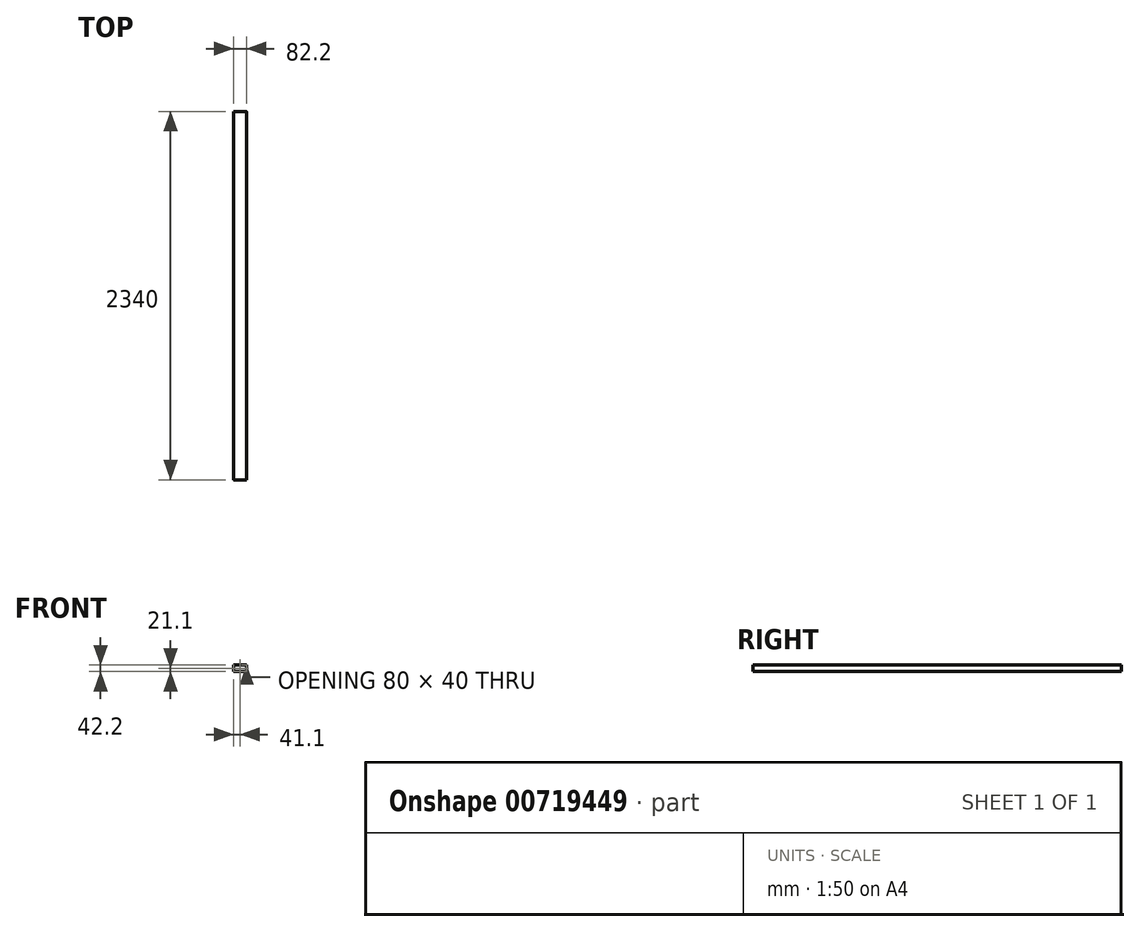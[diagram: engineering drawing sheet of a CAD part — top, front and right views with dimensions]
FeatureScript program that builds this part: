
annotation { "Feature Type Name" : "Feature", "Feature Type Description" : "" }
export const myFeature = defineFeature(function(context is Context, id is Id, definition is map)
    precondition{}
    {
        {
            var Q0;
            Q0=qCreatedBy(makeId("Front.planeOp"),FACE);
            var sketch = newSketch(context, id + "F0", { "sketchPlane" : qUnion([Q0])});
            skLineSegment(sketch, "E0.bottom", {"start": v(-35, 20) * mm, "end": v(35, 20) * mm});
            skLineSegment(sketch, "E0.top", {"start": v(-35, -20) * mm, "end": v(35, -20) * mm});
            skLineSegment(sketch, "E0.left", {"start": v(-40, 15) * mm, "end": v(-40, -15) * mm});
            skLineSegment(sketch, "E0.right", {"start": v(40, 15) * mm, "end": v(40, -15) * mm});
            skPoint(sketch, "E1.visualSharp", {"position": v(-40, 20) * mm});
            skArc(sketch, "E1.filletArc", {"start": v(-35, 20) * mm, "mid": v(-38.54, 18.54) * mm, "end": v(-40, 15) * mm});
            skPoint(sketch, "E2.visualSharp", {"position": v(40, 20) * mm});
            skArc(sketch, "E2.filletArc", {"start": v(40, 15) * mm, "mid": v(38.54, 18.54) * mm, "end": v(35, 20) * mm});
            skPoint(sketch, "E3.visualSharp", {"position": v(40, -20) * mm});
            skArc(sketch, "E3.filletArc", {"start": v(35, -20) * mm, "mid": v(38.54, -18.54) * mm, "end": v(40, -15) * mm});
            skPoint(sketch, "E4.visualSharp", {"position": v(-40, -20) * mm});
            skArc(sketch, "E4.filletArc", {"start": v(-40, -15) * mm, "mid": v(-38.54, -18.54) * mm, "end": v(-35, -20) * mm});
            skLineSegment(sketch, "E5.0", {"start": v(41.1, 16.1) * mm, "end": v(41.1, -16.1) * mm});
            skLineSegment(sketch, "E5.1", {"start": v(-36.1, 21.1) * mm, "end": v(36.1, 21.1) * mm});
            skLineSegment(sketch, "E5.2", {"start": v(-41.1, 16.1) * mm, "end": v(-41.1, -16.1) * mm});
            skLineSegment(sketch, "E5.3", {"start": v(-36.1, -21.1) * mm, "end": v(36.1, -21.1) * mm});
            skPoint(sketch, "E6.visualSharp", {"position": v(-41.1, 21.1) * mm});
            skArc(sketch, "E6.filletArc", {"start": v(-36.1, 21.1) * mm, "mid": v(-39.64, 19.64) * mm, "end": v(-41.1, 16.1) * mm});
            skPoint(sketch, "E7.visualSharp", {"position": v(41.1, 21.1) * mm});
            skArc(sketch, "E7.filletArc", {"start": v(41.1, 16.1) * mm, "mid": v(39.64, 19.64) * mm, "end": v(36.1, 21.1) * mm});
            skPoint(sketch, "E8.visualSharp", {"position": v(41.1, -21.1) * mm});
            skArc(sketch, "E8.filletArc", {"start": v(36.1, -21.1) * mm, "mid": v(39.64, -19.64) * mm, "end": v(41.1, -16.1) * mm});
            skPoint(sketch, "E9.visualSharp", {"position": v(-41.1, -21.1) * mm});
            skArc(sketch, "E9.filletArc", {"start": v(-41.1, -16.1) * mm, "mid": v(-39.64, -19.64) * mm, "end": v(-36.1, -21.1) * mm});
            skSolve(sketch);
        }
        {
            var Q0;
            Q0=makeQuery(id+"F0.imprint","IMPRINT",FACE,{"disambiguationData":[TD([[makeQuery(id+"F0.imprint","IMPRINT",EDGE,{"derivedFrom":sQuery(id+"F0.wireOp",EDGE,"E0.bottom")}),1.0]])]});
            extrude(context, id + "F1", {"entities" : qUnion([Q0]), "depth" : 2340 * mm, "offsetDistance" : 25 * mm});
        }
        {
            var Q0;
            Q0=qCreatedBy(makeId("Front.planeOp"),FACE);
            var sketch = newSketch(context, id + "F2", { "sketchPlane" : qUnion([Q0])});
            skPoint(sketch, "E10", {"position": v(0, 0) * mm});
            skSolve(sketch);
        }
    });
